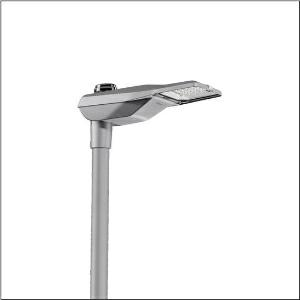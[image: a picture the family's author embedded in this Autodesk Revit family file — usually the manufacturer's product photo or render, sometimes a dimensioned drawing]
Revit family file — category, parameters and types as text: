
# Revit family: streetlight_sl_21_micro___st1_5a_5xe5p47n08db_8f26
name_source: partatom
category: Lighting Fixtures
units: mm (PartAtom-declared; Revit-internal decimal feet)

## family parameters
Cut with Voids When Loaded = No
Host = Face
Light Source = No
Part Type = Normal
Room Calculation Point = No
Round Connector Dimension = Use Diameter
Shared = No

## types (1)
- --- (1 x LED, 5230 lm, 39.1 W, 4000K)
    Apparent Load = 39 VA
    CIE Flux Codes = 22 53 95 100 100
    Color Rendering = 70
    Color Temperature = 4000K
    Default Elevation = 1800 mm
    Description = Streetlight SL 21 micro, mast luminaire, primary light control with lens, of PMMA, primary optical cover: cover, of toughened safety glass, transparent, light distribution: ST1.5a, light emission: direct distribution, primary light characteristic: asymmetric, installation type: post-top, LED, 3G 1.5mm², High Power LED, rated luminous flux: 5.230lm, luminous efficacy: 134lm/W, light colour: 740, colour temperature: 4000K, control: overheat protection, pre-setting: linear dimming characteristic, constant luminous flux control, time-dependent luminous flux control, flexible luminous flux parameterisation, mains connection: 230..240V, AC, 50/60Hz, connection cable pre-assembled, cable length: 6,5m, wiring characteristics: H07RN-F, start of lifetime: 39W, end of service life: 41W, reduction: 18W, luminaire housing, of diecast aluminium (EN AC-44300), powder-coated, Siteco® metallic grey (DB 702S), corrosivity category C5 mid according to DIN EN ISO 12944, multi-level sealing system, sealing non-destructively replaceable, inclination adjustable: 0°, 5°, 10°, 15°, length: 528mm, width: 235mm, height: 110mm, spigot size: 76/60mm (post-top), protection rating (complete): IP66, insulation class (complete): insulation class I (protective earthing), certification: CE, ENEC, ENEC+, VDE, impact resistance: IK09, permissible operating ambient temperature for outdoor applications: -40..+50°C, standard-compliant lighting for roads and squares, packaging unit: 1 piece

Light Distribution: ST1.5a
    Height = 110 mm
    Lamp = 1 x LED
    Lamp Light Flux = 5230 lm
    Lamp Power = 39.1 W
    Lamp count = 1
    Length = 528 mm
    Luminous efficacy = 134 lm/W
    Manufacturer = Siteco
    ModVariant = No
    Model = 5XE5P47N08DB
    Number of Poles = 1
    OnlyDefault = Yes
    Power Factor = 1
    Product Name = Streetlight SL 21 micro | ST1.5a
    Product group = mast luminaire | pylon top
    ProductGroupID = 6100
    Protection Class = Protection class I
    Protection Degree = IP 66
    RLX_Detail_Level = 1
    RLX_Emergency_Light_Flux = 0 lm
    RLX_Emergency_Type = 0
    RLX_Emergency_Type_DB = No
    RlxData = <blob elided: 102761 chars, md5=74d2819b>
    Socket = socket
    Standby Power = 0 W
    System Light Flux = 5230 lm
    System Power = 39 W
    Type Comments = factory setting: luminous flux: 100 % | dim-lin: 254 | 765 mA
    Type Image = l_1294375.jpg
    URL = http://relux.com
    VarID = @adj_103499
    Voltage = 0 V
    Weight = 0.00 kg
    Width = 235 mm

## geometry (parser evidence)
native form markers: Blend x4, Sweep x9
no freeform markers — native parametric forms only
